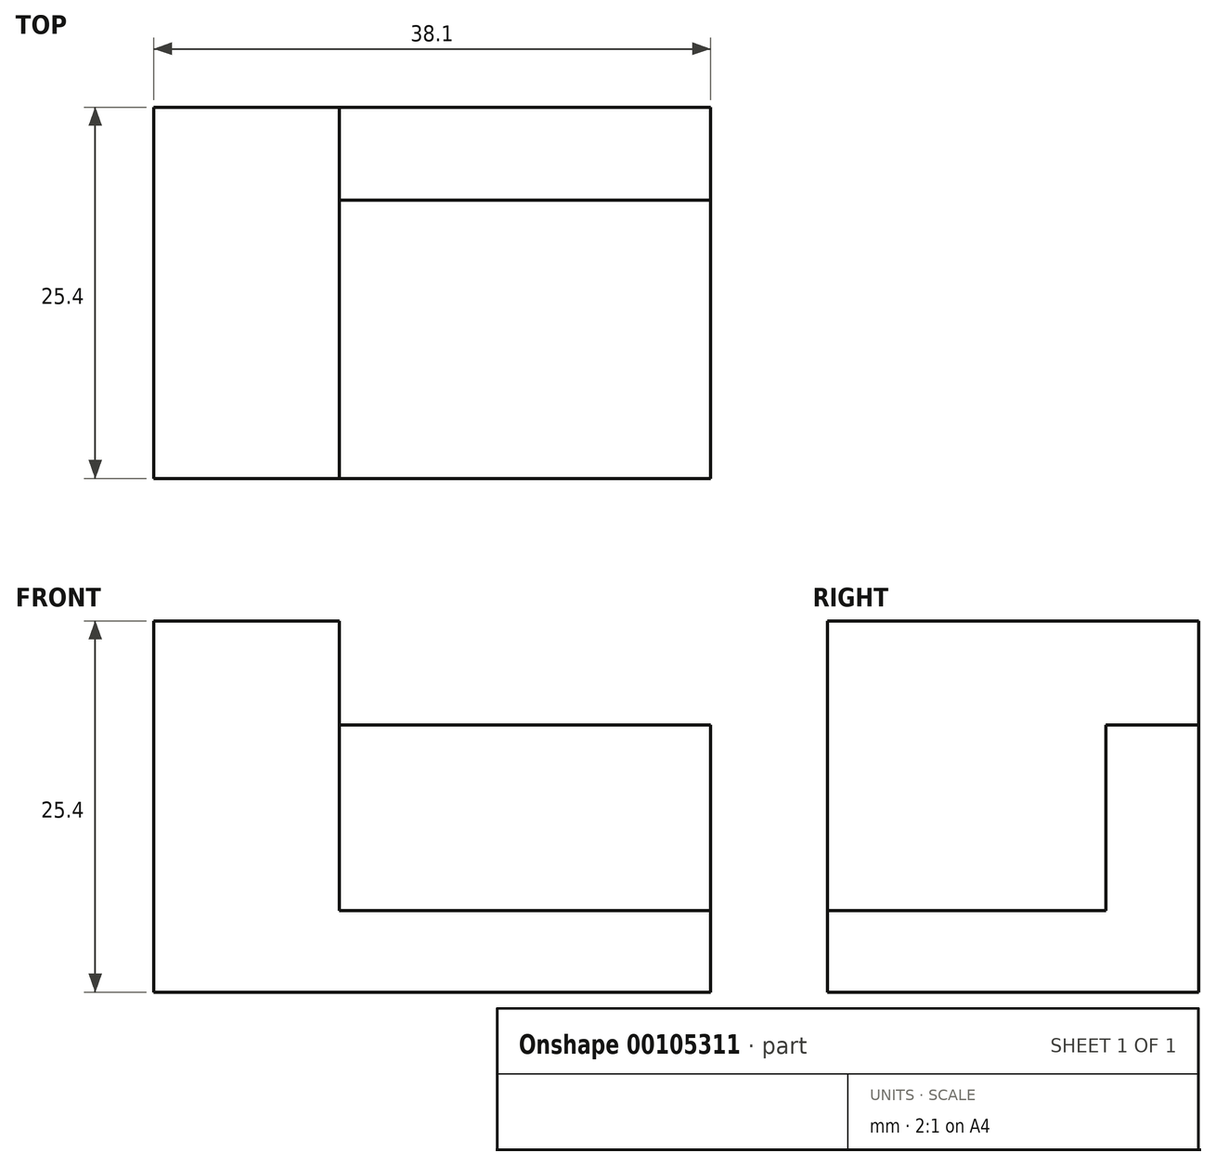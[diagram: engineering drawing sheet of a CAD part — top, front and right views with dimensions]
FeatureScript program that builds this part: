
annotation { "Feature Type Name" : "Feature", "Feature Type Description" : "" }
export const myFeature = defineFeature(function(context is Context, id is Id, definition is map)
    precondition{}
    {
        {
            var Q0;
            Q0=qCreatedBy(makeId("Front.planeOp"),FACE);
            var sketch = newSketch(context, id + "F0", { "sketchPlane" : qUnion([Q0])});
            skLineSegment(sketch, "E0.bottom", {"start": v(0, 0) * mm, "end": v(38.1, 0) * mm});
            skLineSegment(sketch, "E0.top", {"start": v(0, 25.4) * mm, "end": v(12.7, 25.4) * mm});
            skLineSegment(sketch, "E0.left", {"start": v(0, 0) * mm, "end": v(0, 25.4) * mm});
            skLineSegment(sketch, "E0.right", {"start": v(38.1, 0) * mm, "end": v(38.1, 18.28) * mm});
            skLineSegment(sketch, "E1.top", {"start": v(12.7, 5.58) * mm, "end": v(12.7, 5.58) * mm});
            skLineSegment(sketch, "E1.right", {"start": v(12.7, 25.4) * mm, "end": v(12.7, 5.58) * mm});
            skLineSegment(sketch, "E2.bottom", {"start": v(38.1, 18.28) * mm, "end": v(12.7, 18.28) * mm});
            skLineSegment(sketch, "E2.top", {"start": v(38.1, 5.58) * mm, "end": v(12.7, 5.58) * mm});
            skLineSegment(sketch, "E2.left", {"start": v(38.1, 18.28) * mm, "end": v(38.1, 5.58) * mm});
            skLineSegment(sketch, "E2.right", {"start": v(12.7, 18.28) * mm, "end": v(12.7, 5.58) * mm});
            skSolve(sketch);
        }
        {
            var Q0;
            Q0=makeQuery(id+"F0.imprint","IMPRINT",FACE,{"disambiguationData":[TD([[makeQuery(id+"F0.imprint","IMPRINT",EDGE,{"derivedFrom":sQuery(id+"F0.wireOp",EDGE,"E0.bottom")}),1.0]])]});
            extrude(context, id + "F1", {"entities" : qUnion([Q0]), "depth" : 25.4 * mm});
        }
        {
            var Q0;
            Q0=makeQuery(id+"F0.imprint","IMPRINT",FACE,{"disambiguationData":[TD([[makeQuery(id+"F0.imprint","IMPRINT",EDGE,{"derivedFrom":sQuery(id+"F0.wireOp",EDGE,"E2.bottom")}),1.0]])]});
            extrude(context, id + "F2", {"entities" : qUnion([Q0]), "operationType" : NewBodyOperationType.ADD, "depth" : 6.35 * mm});
        }
    });
